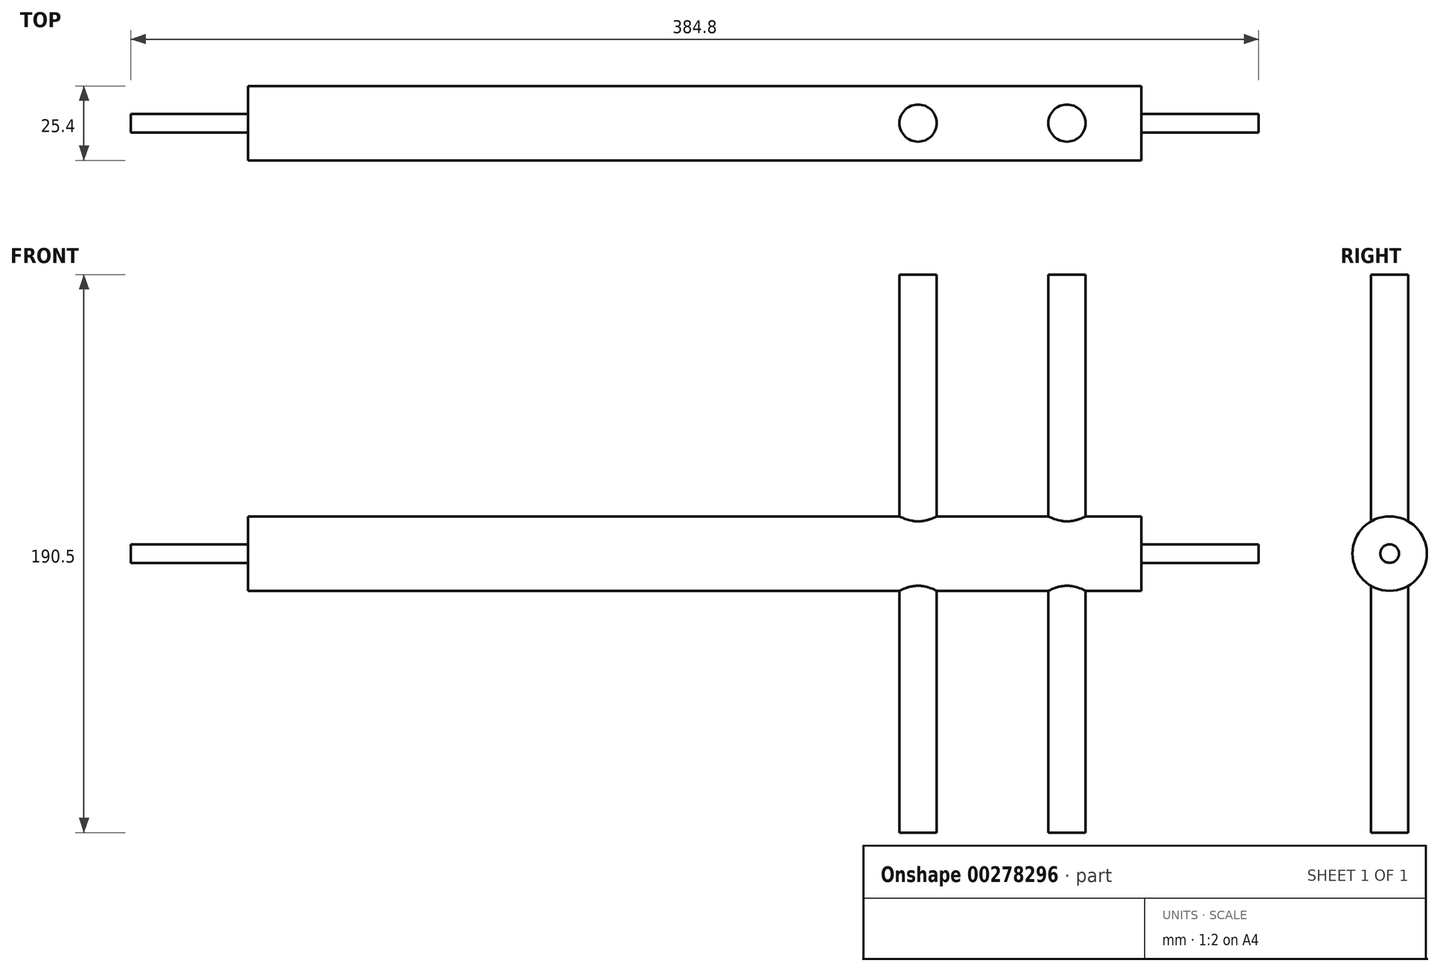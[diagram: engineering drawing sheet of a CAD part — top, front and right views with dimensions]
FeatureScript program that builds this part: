
annotation { "Feature Type Name" : "Feature", "Feature Type Description" : "" }
export const myFeature = defineFeature(function(context is Context, id is Id, definition is map)
    precondition{}
    {
        {
            var Q0;
            Q0=qCreatedBy(makeId("Right.planeOp"),FACE);
            var sketch = newSketch(context, id + "F0", { "sketchPlane" : qUnion([Q0])});
            skCircle(sketch, "E0", {"center": v(0, 0) * mm, "radius": 12.7 * mm});
            skSolve(sketch);
        }
        {
            var Q0;
            Q0=qSketchRegion(id+"F0",true);
            extrude(context, id + "F1", {"entities" : qUnion([Q0]), "depth" : 304.8 * mm});
        }
        {
            var Q0;
            Q0=makeQuery(id+"F1.opExtrude","CAP_FACE",FACE,{"disambiguationData":[OSD([sQuery(id+"F0.wireOp",EDGE,"E0")])],"isStart":false});
            var sketch = newSketch(context, id + "F2", { "sketchPlane" : qUnion([Q0])});
            skCircle(sketch, "E1", {"center": v(0, 0) * mm, "radius": 3.18 * mm});
            skSolve(sketch);
        }
        {
            var Q0;
            Q0=qSketchRegion(id+"F2",true);
            extrude(context, id + "F3", {"entities" : qUnion([Q0]), "operationType" : NewBodyOperationType.ADD, "depth" : 40 * mm});
        }
        {
            var Q0;
            Q0=makeQuery(id+"F1.opExtrude","CAP_FACE",FACE,{"disambiguationData":[OSD([sQuery(id+"F0.wireOp",EDGE,"E0")])],"isStart":true});
            var sketch = newSketch(context, id + "F4", { "sketchPlane" : qUnion([Q0])});
            skCircle(sketch, "E2", {"center": v(0, 0) * mm, "radius": 3.18 * mm});
            skSolve(sketch);
        }
        {
            var Q0;
            Q0=qSketchRegion(id+"F4",true);
            extrude(context, id + "F5", {"entities" : qUnion([Q0]), "operationType" : NewBodyOperationType.ADD, "depth" : 40 * mm});
        }
        {
            var Q0;
            Q0=qCreatedBy(makeId("Top.planeOp"),FACE);
            var sketch = newSketch(context, id + "F6", { "sketchPlane" : qUnion([Q0])});
            skCircle(sketch, "E3", {"center": v(228.6, 0) * mm, "radius": 6.35 * mm});
            skLineSegment(sketch, "E4", {"start": v(228.6, 0) * mm, "end": v(177.8, 0) * mm});
            skLineSegment(sketch, "E5", {"start": v(177.8, 0) * mm, "end": v(127, 0) * mm});
            skLineSegment(sketch, "E6", {"start": v(127, 0) * mm, "end": v(76.2, 0) * mm});
            skLineSegment(sketch, "E7", {"start": v(0, 0) * mm, "end": v(76.2, 0) * mm});
            skLineSegment(sketch, "E8", {"start": v(228.6, 0) * mm, "end": v(279.4, 0) * mm});
            skCircle(sketch, "E9", {"center": v(279.4, 0) * mm, "radius": 6.35 * mm});
            skSolve(sketch);
        }
        {
            var Q0;
            Q0=qSketchRegion(id+"F6",true);
            extrude(context, id + "F7", {"entities" : qUnion([Q0]), "operationType" : NewBodyOperationType.ADD, "depth" : 95.25 * mm, "hasSecondDirection" : true, "secondDirectionOppositeDirection" : true, "secondDirectionDepth" : 95.25 * mm});
        }
    });
